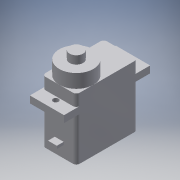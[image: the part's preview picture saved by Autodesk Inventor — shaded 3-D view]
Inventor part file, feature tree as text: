
AUTODESK INVENTOR PART (.ipt)
format: ipt  version: 2018 (Build 220112000, 112)  size: 160,256 bytes
history: native  units: in
note: dims shown in document units (in); Inventor stores cm internally (conversion verified against a paired STEP export)
features: extrude x5, sketch x5, plane x1
ambient origin geometry x8: Origin, YZ Plane, XZ Plane, XY Plane, X Axis, Y Axis, Z Axis, Center Point
bodies: Solid1 (feature_tree)
feature tree (11):
  extrude  "Extrusion1"  Depth=0.9in
  extrude  "Extrusion2"  Depth=0.9in TaperAngle=0.0deg
  plane  "Work Plane1"
  extrude  "Extrusion4"  [1 undecoded]
  extrude  "Extrusion5"  Depth=0.08in
  extrude  "Extrusion6"  Depth=0.1in TaperAngle=0.0deg
  sketch  "Sketch1"  dims[d0=0.5in d1=0.9in]
  sketch  "Sketch2"  dims[d2=0.05in d3=0.9in d4=0.0in]
  sketch  "Sketch5"  dims[d7=0.2in d8=0.0in d12=-0.17in]
  sketch  "Sketch6"  dims[d13=0.63in d14=0.08in]
  sketch  "Sketch7"  dims[d15=1.0in d16=0.1in d17=0.0in d18=0.13in d19=0.04in d20=0.17in d21=0.1in d22=0.0in d23=0.1969in d24=0.1181in d25=0.0in]
note: 1 required parameter value undecoded (feature->parameter linkage not recoverable at this tier; creation-order binding heuristic only, values carry confidence <= 0.55)
